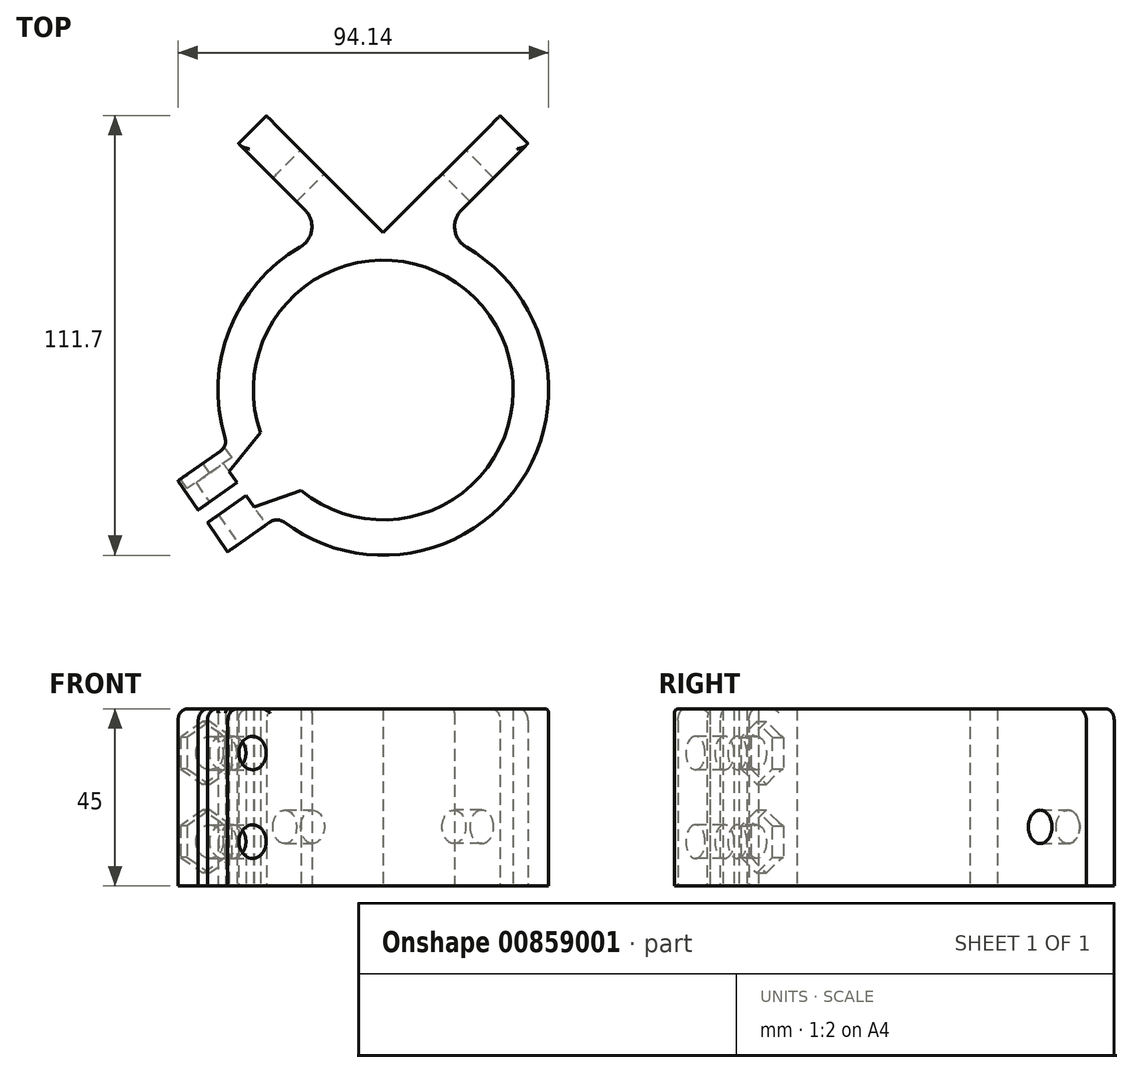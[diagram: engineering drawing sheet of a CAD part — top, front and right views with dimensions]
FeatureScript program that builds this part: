
annotation { "Feature Type Name" : "Feature", "Feature Type Description" : "" }
export const myFeature = defineFeature(function(context is Context, id is Id, definition is map)
    precondition{}
    {
        {
            var Q0;
            Q0=qCreatedBy(makeId("Top.planeOp"),FACE);
            var sketch = newSketch(context, id + "F0", { "sketchPlane" : qUnion([Q0])});
            skLineSegment(sketch, "E0", {"start": v(0, 0) * mm, "end": v(-29.7, 29.7) * mm});
            skLineSegment(sketch, "E1", {"start": v(0, 38.94) * mm, "end": v(0, 0) * mm, "construction": true});
            skLineSegment(sketch, "E2", {"start": v(-29.7, 29.7) * mm, "end": v(-36.77, 22.63) * mm});
            skLineSegment(sketch, "E3", {"start": v(-36.77, 22.63) * mm, "end": v(-13.8, -0.33) * mm});
            skLineSegment(sketch, "E4", {"start": v(0, 0) * mm, "end": v(0, -40) * mm, "construction": true});
            skArc(sketch, "E5", {"start": v(-25.84, -60.53) * mm, "mid": v(27.03, -21.07) * mm, "end": v(-28.13, -57.25) * mm});
            skArc(sketch, "E6", {"start": v(-33.22, -65.7) * mm, "mid": v(34.1, -64.53) * mm, "end": v(13.8, -0.33) * mm});
            skLineSegment(sketch, "E7", {"start": v(0, -40) * mm, "end": v(-34.4, -64.1) * mm, "construction": true});
            skLineSegment(sketch, "E8", {"start": v(-35.51, -62.42) * mm, "end": v(-46.98, -70.45) * mm});
            skLineSegment(sketch, "E9", {"start": v(-46.98, -70.45) * mm, "end": v(-52.14, -63.08) * mm});
            skLineSegment(sketch, "E10", {"start": v(-52.14, -63.08) * mm, "end": v(-39.51, -54.24) * mm});
            skLineSegment(sketch, "E11.MirrorCS", {"start": v(-44.69, -73.73) * mm, "end": v(-39.52, -81.1) * mm});
            skLineSegment(sketch, "E12.MirrorCS", {"start": v(-39.52, -81.1) * mm, "end": v(-26.9, -72.26) * mm});
            skLineSegment(sketch, "E13.MirrorCS", {"start": v(-33.22, -65.7) * mm, "end": v(-44.69, -73.73) * mm});
            skLineSegment(sketch, "E14", {"start": v(-35.51, -62.42) * mm, "end": v(-28.13, -57.25) * mm});
            skLineSegment(sketch, "E15.MirrorCS", {"start": v(-33.22, -65.7) * mm, "end": v(-25.84, -60.53) * mm});
            skLineSegment(sketch, "E16.MirrorCS", {"start": v(29.7, 29.7) * mm, "end": v(36.77, 22.63) * mm});
            skLineSegment(sketch, "E17.MirrorCS", {"start": v(0, 0) * mm, "end": v(29.7, 29.7) * mm});
            skLineSegment(sketch, "E18.MirrorCS", {"start": v(36.77, 22.63) * mm, "end": v(13.8, -0.33) * mm});
            skPoint(sketch, "E19.orphan", {"position": v(0, -14.14) * mm});
            skArc(sketch, "E20.trimOffspring", {"start": v(-13.8, -0.33) * mm, "mid": v(-39.65, -26.14) * mm, "end": v(-35.51, -62.42) * mm});
            skLineSegment(sketch, "E21", {"start": v(-31.17, -50.84) * mm, "end": v(-39.15, -60.7) * mm});
            skLineSegment(sketch, "E22.MirrorCS", {"start": v(-20.85, -65.58) * mm, "end": v(-32.84, -69.7) * mm});
            skLineSegment(sketch, "E23", {"start": v(-39.15, -60.7) * mm, "end": v(-32.84, -69.7) * mm});
            skSolve(sketch);
        }
        {
            var Q0;
            Q0=makeQuery(id+"F0.imprint","IMPRINT",FACE,{"disambiguationData":[TD([[makeQuery(id+"F0.imprint","IMPRINT",EDGE,{"derivedFrom":sQuery(id+"F0.wireOp",EDGE,"E0")}),1.0]])]});
            var Q1;
            {var subQ4=sQuery(id+"F0.wireOp",EDGE,"E9");Q1=makeQuery(id+"F0.imprint","IMPRINT",FACE,{"disambiguationData":[TD([[makeQuery(id+"F0.imprint","IMPRINT",EDGE,{"derivedFrom":subQ4}),-1.0]])]});}
            var Q2;
            {var subQ1=sQuery(id+"F0.wireOp",EDGE,"E11.MirrorCS");Q2=makeQuery(id+"F0.imprint","IMPRINT",FACE,{"disambiguationData":[TD([[makeQuery(id+"F0.imprint","IMPRINT",EDGE,{"derivedFrom":subQ1}),1.0]])]});}
            extrude(context, id + "F1", {"entities" : qUnion([Q0, Q1, Q2]), "depth" : 45 * mm, "offsetDistance" : 25 * mm});
        }
        {
            var Q0;
            Q0=makeQuery(id+"F1.opExtrude","SWEPT_FACE",FACE,{"disambiguationData":[OSD([sQuery(id+"F0.wireOp",EDGE,"E17.MirrorCS")])]});
            var sketch = newSketch(context, id + "F2", { "sketchPlane" : qUnion([Q0])});
            skLineSegment(sketch, "E24", {"start": v(0, 15) * mm, "end": v(-50.8, 15) * mm, "construction": true});
            skCircle(sketch, "E25", {"center": v(-25.4, 15) * mm, "radius": 4.25 * mm});
            skSolve(sketch);
        }
        {
            var Q0;
            Q0=qSketchRegion(id+"F2",true);
            extrude(context, id + "F3", {"entities" : qUnion([Q0]), "operationType" : NewBodyOperationType.REMOVE, "endBound" : BoundingType.UP_TO_NEXT, "oppositeDirection" : true, "depth" : 25 * mm, "offsetDistance" : 25 * mm});
        }
        {
            var Q0;
            Q0=makeQuery(id+"F1.opExtrude","SWEPT_FACE",FACE,{"disambiguationData":[OSD([sQuery(id+"F0.wireOp",EDGE,"E0")])]});
            var sketch = newSketch(context, id + "F4", { "sketchPlane" : qUnion([Q0])});
            skLineSegment(sketch, "E26", {"start": v(0, 15) * mm, "end": v(50.8, 15) * mm, "construction": true});
            skCircle(sketch, "E27", {"center": v(25.4, 15) * mm, "radius": 4.25 * mm});
            skSolve(sketch);
        }
        {
            var Q0;
            Q0=qSketchRegion(id+"F4",true);
            extrude(context, id + "F5", {"entities" : qUnion([Q0]), "operationType" : NewBodyOperationType.REMOVE, "endBound" : BoundingType.UP_TO_NEXT, "oppositeDirection" : true, "depth" : 25 * mm, "offsetDistance" : 25 * mm});
        }
        {
            var Q0;
            Q0=makeQuery(id+"F1.opExtrude","SWEPT_FACE",FACE,{"disambiguationData":[OSD([sQuery(id+"F0.wireOp",EDGE,"E12.MirrorCS")])]});
            var sketch = newSketch(context, id + "F6", { "sketchPlane" : qUnion([Q0])});
            skLineSegment(sketch, "E28", {"start": v(-71.19, 45) * mm, "end": v(-71.19, 0) * mm, "construction": true});
            skLineSegment(sketch, "E29", {"start": v(-78.9, 22.5) * mm, "end": v(-63.48, 22.5) * mm, "construction": true});
            skLineSegment(sketch, "E30", {"start": v(-78.9, 22.5) * mm, "end": v(-63.48, 45) * mm, "construction": true});
            skCircle(sketch, "E31", {"center": v(-71.19, 33.75) * mm, "radius": 4.25 * mm});
            skCircle(sketch, "E32.MirrorC", {"center": v(-71.19, 11.25) * mm, "radius": 4.25 * mm});
            skLineSegment(sketch, "E33.MirrorCS", {"start": v(-78.9, 22.5) * mm, "end": v(-63.48, 0) * mm, "construction": true});
            skSolve(sketch);
        }
        {
            var Q0;
            Q0=qSketchRegion(id+"F6",true);
            var Q1;
            Q1=makeQuery(id+"F1.opExtrude","SWEPT_FACE",FACE,{"disambiguationData":[OSD([sQuery(id+"F0.wireOp",EDGE,"E10")])]});
            extrude(context, id + "F7", {"entities" : qUnion([Q0]), "operationType" : NewBodyOperationType.REMOVE, "endBound" : BoundingType.UP_TO_SURFACE, "oppositeDirection" : true, "depth" : 25 * mm, "endBoundEntityFace" : qUnion([Q1]), "offsetDistance" : 25 * mm});
        }
        {
            var Q0;
            Q0=makeQuery(id+"F1.opExtrude","SWEPT_FACE",FACE,{"disambiguationData":[OSD([sQuery(id+"F0.wireOp",EDGE,"E10")])]});
            var sketch = newSketch(context, id + "F8", { "sketchPlane" : qUnion([Q0])});
            skCircle(sketch, "E34.cCircle", {"center": v(71.19, 33.75) * mm, "radius": 6.92 * mm, "construction": true});
            skLineSegment(sketch, "E34.0", {"start": v(71.19, 41.75) * mm, "end": v(78.11, 37.75) * mm});
            skLineSegment(sketch, "E34.1", {"start": v(78.11, 37.75) * mm, "end": v(78.11, 29.75) * mm});
            skLineSegment(sketch, "E34.2", {"start": v(78.11, 29.75) * mm, "end": v(71.19, 25.75) * mm});
            skLineSegment(sketch, "E34.3", {"start": v(71.19, 25.75) * mm, "end": v(64.26, 29.75) * mm});
            skLineSegment(sketch, "E34.4", {"start": v(64.26, 29.75) * mm, "end": v(64.26, 37.75) * mm});
            skLineSegment(sketch, "E34.5", {"start": v(64.26, 37.75) * mm, "end": v(71.19, 41.75) * mm});
            skPoint(sketch, "E34.0.midPoint", {"position": v(74.65, 39.75) * mm});
            skCircle(sketch, "E35.cCircle", {"center": v(71.19, 11.25) * mm, "radius": 6.92 * mm, "construction": true});
            skLineSegment(sketch, "E35.0", {"start": v(64.26, 15.25) * mm, "end": v(71.19, 19.25) * mm});
            skLineSegment(sketch, "E35.1", {"start": v(71.19, 19.25) * mm, "end": v(78.11, 15.25) * mm});
            skLineSegment(sketch, "E35.2", {"start": v(78.11, 15.25) * mm, "end": v(78.11, 7.25) * mm});
            skLineSegment(sketch, "E35.3", {"start": v(78.11, 7.25) * mm, "end": v(71.19, 3.25) * mm});
            skLineSegment(sketch, "E35.4", {"start": v(71.19, 3.25) * mm, "end": v(64.26, 7.25) * mm});
            skLineSegment(sketch, "E35.5", {"start": v(64.26, 7.25) * mm, "end": v(64.26, 15.25) * mm});
            skPoint(sketch, "E35.0.midPoint", {"position": v(67.72, 17.25) * mm});
            skSolve(sketch);
        }
        {
            var Q0;
            Q0=qSketchRegion(id+"F8",true);
            extrude(context, id + "F9", {"entities" : qUnion([Q0]), "operationType" : NewBodyOperationType.REMOVE, "oppositeDirection" : true, "depth" : 3 * mm, "offsetDistance" : 25 * mm});
        }
        {
            var Q0;
            Q0=makeQuery(id+"F1.opExtrude","SWEPT_EDGE",EDGE,{"disambiguationData":[OSD([sQuery(id+"F0.wireOp",EDGE,"E3"),sQuery(id+"F0.wireOp",EDGE,"E20.trimOffspring")])]});
            var Q1;
            Q1=makeQuery(id+"F1.opExtrude","SWEPT_EDGE",EDGE,{"disambiguationData":[OSD([sQuery(id+"F0.wireOp",EDGE,"E6"),sQuery(id+"F0.wireOp",EDGE,"E18.MirrorCS")])]});
            fillet(context, id + "F10", {"entities" : qUnion([Q0, Q1]), "radius" : 6 * mm, "tangentPropagation" : true, "allowEdgeOverflow" : false});
        }
        {
            var Q0;
            Q0=makeQuery(id+"F1.opExtrude","CAP_EDGE",EDGE,{"disambiguationData":[OSD([sQuery(id+"F0.wireOp",EDGE,"E9")])],"isStart":false});
            var Q1;
            Q1=makeQuery(id+"F1.opExtrude","CAP_EDGE",EDGE,{"disambiguationData":[OSD([sQuery(id+"F0.wireOp",EDGE,"E11.MirrorCS")])],"isStart":false});
            var Q2;
            Q2=makeQuery(id+"F1.opExtrude","CAP_EDGE",EDGE,{"disambiguationData":[OSD([sQuery(id+"F0.wireOp",EDGE,"E2")])],"isStart":false});
            var Q3;
            Q3=makeQuery(id+"F1.opExtrude","CAP_EDGE",EDGE,{"disambiguationData":[OSD([sQuery(id+"F0.wireOp",EDGE,"E16.MirrorCS")])],"isStart":false});
            var Q4;
            Q4=makeQuery(id+"F1.opExtrude","SWEPT_EDGE",EDGE,{"disambiguationData":[OSD([sQuery(id+"F0.wireOp",EDGE,"E10"),sQuery(id+"F0.wireOp",EDGE,"E20.trimOffspring")])]});
            var Q5;
            Q5=makeQuery(id+"F1.opExtrude","SWEPT_EDGE",EDGE,{"disambiguationData":[OSD([sQuery(id+"F0.wireOp",EDGE,"E6"),sQuery(id+"F0.wireOp",EDGE,"E12.MirrorCS")])]});
            fillet(context, id + "F11", {"entities" : qUnion([Q0, Q1, Q2, Q3, Q4, Q5]), "radius" : 3 * mm, "tangentPropagation" : true, "allowEdgeOverflow" : false});
        }
        {
            var Q0;
            Q0=makeQuery(id+"F1.opExtrude","CAP_EDGE",EDGE,{"disambiguationData":[OSD([sQuery(id+"F0.wireOp",EDGE,"E6")])],"isStart":false});
            var Q1;
            {var subQ0=sQuery(id+"F0.wireOp",EDGE,"E12.MirrorCS");var subQ1=sQuery(id+"F0.wireOp",EDGE,"E6");Q1=makeQuery(id+"F11.opFillet","BLEND_EDGE",EDGE,{"blendedFrom":[makeQuery(id+"F1.opExtrude","SWEPT_EDGE",EDGE,{"disambiguationData":[OSD([subQ1,subQ0])]}),makeQuery(id+"F1.opExtrude","CAP_FACE",FACE,{"disambiguationData":[OSD([sQuery(id+"F0.wireOp",EDGE,"E0"),sQuery(id+"F0.wireOp",EDGE,"E2"),sQuery(id+"F0.wireOp",EDGE,"E3"),sQuery(id+"F0.wireOp",EDGE,"E5"),subQ1,sQuery(id+"F0.wireOp",EDGE,"E8"),sQuery(id+"F0.wireOp",EDGE,"E9"),sQuery(id+"F0.wireOp",EDGE,"E10"),sQuery(id+"F0.wireOp",EDGE,"E11.MirrorCS"),subQ0,sQuery(id+"F0.wireOp",EDGE,"E13.MirrorCS"),sQuery(id+"F0.wireOp",EDGE,"E16.MirrorCS"),sQuery(id+"F0.wireOp",EDGE,"E17.MirrorCS"),sQuery(id+"F0.wireOp",EDGE,"E18.MirrorCS"),sQuery(id+"F0.wireOp",EDGE,"E20.trimOffspring"),sQuery(id+"F0.wireOp",EDGE,"E21"),sQuery(id+"F0.wireOp",EDGE,"E22.MirrorCS"),sQuery(id+"F0.wireOp",EDGE,"E23")])],"isStart":false})],"blendedInto":[makeQuery(id+"F1.opExtrude","CAP_FACE",FACE,{"disambiguationData":[OSD([sQuery(id+"F0.wireOp",EDGE,"E0"),sQuery(id+"F0.wireOp",EDGE,"E2"),sQuery(id+"F0.wireOp",EDGE,"E3"),sQuery(id+"F0.wireOp",EDGE,"E5"),subQ1,sQuery(id+"F0.wireOp",EDGE,"E8"),sQuery(id+"F0.wireOp",EDGE,"E9"),sQuery(id+"F0.wireOp",EDGE,"E10"),sQuery(id+"F0.wireOp",EDGE,"E11.MirrorCS"),subQ0,sQuery(id+"F0.wireOp",EDGE,"E13.MirrorCS"),sQuery(id+"F0.wireOp",EDGE,"E16.MirrorCS"),sQuery(id+"F0.wireOp",EDGE,"E17.MirrorCS"),sQuery(id+"F0.wireOp",EDGE,"E18.MirrorCS"),sQuery(id+"F0.wireOp",EDGE,"E20.trimOffspring"),sQuery(id+"F0.wireOp",EDGE,"E21"),sQuery(id+"F0.wireOp",EDGE,"E22.MirrorCS"),sQuery(id+"F0.wireOp",EDGE,"E23")])],"isStart":false})]});}
            var Q2;
            {var subQ0=sQuery(id+"F0.wireOp",EDGE,"E20.trimOffspring");var subQ1=sQuery(id+"F0.wireOp",EDGE,"E3");Q2=makeQuery(id+"F10.opFillet","BLEND_EDGE",EDGE,{"blendedFrom":[makeQuery(id+"F1.opExtrude","SWEPT_EDGE",EDGE,{"disambiguationData":[OSD([subQ1,subQ0])]}),makeQuery(id+"F1.opExtrude","CAP_FACE",FACE,{"disambiguationData":[OSD([sQuery(id+"F0.wireOp",EDGE,"E0"),sQuery(id+"F0.wireOp",EDGE,"E2"),subQ1,sQuery(id+"F0.wireOp",EDGE,"E5"),sQuery(id+"F0.wireOp",EDGE,"E6"),sQuery(id+"F0.wireOp",EDGE,"E8"),sQuery(id+"F0.wireOp",EDGE,"E9"),sQuery(id+"F0.wireOp",EDGE,"E10"),sQuery(id+"F0.wireOp",EDGE,"E11.MirrorCS"),sQuery(id+"F0.wireOp",EDGE,"E12.MirrorCS"),sQuery(id+"F0.wireOp",EDGE,"E13.MirrorCS"),sQuery(id+"F0.wireOp",EDGE,"E16.MirrorCS"),sQuery(id+"F0.wireOp",EDGE,"E17.MirrorCS"),sQuery(id+"F0.wireOp",EDGE,"E18.MirrorCS"),subQ0,sQuery(id+"F0.wireOp",EDGE,"E21"),sQuery(id+"F0.wireOp",EDGE,"E22.MirrorCS"),sQuery(id+"F0.wireOp",EDGE,"E23")])],"isStart":false})],"blendedInto":[makeQuery(id+"F1.opExtrude","CAP_FACE",FACE,{"disambiguationData":[OSD([sQuery(id+"F0.wireOp",EDGE,"E0"),sQuery(id+"F0.wireOp",EDGE,"E2"),subQ1,sQuery(id+"F0.wireOp",EDGE,"E5"),sQuery(id+"F0.wireOp",EDGE,"E6"),sQuery(id+"F0.wireOp",EDGE,"E8"),sQuery(id+"F0.wireOp",EDGE,"E9"),sQuery(id+"F0.wireOp",EDGE,"E10"),sQuery(id+"F0.wireOp",EDGE,"E11.MirrorCS"),sQuery(id+"F0.wireOp",EDGE,"E12.MirrorCS"),sQuery(id+"F0.wireOp",EDGE,"E13.MirrorCS"),sQuery(id+"F0.wireOp",EDGE,"E16.MirrorCS"),sQuery(id+"F0.wireOp",EDGE,"E17.MirrorCS"),sQuery(id+"F0.wireOp",EDGE,"E18.MirrorCS"),subQ0,sQuery(id+"F0.wireOp",EDGE,"E21"),sQuery(id+"F0.wireOp",EDGE,"E22.MirrorCS"),sQuery(id+"F0.wireOp",EDGE,"E23")])],"isStart":false})]});}
            var Q3;
            Q3=makeQuery(id+"F1.opExtrude","CAP_EDGE",EDGE,{"disambiguationData":[OSD([sQuery(id+"F0.wireOp",EDGE,"E3")])],"isStart":false});
            var Q4;
            Q4=makeQuery(id+"F1.opExtrude","CAP_EDGE",EDGE,{"disambiguationData":[OSD([sQuery(id+"F0.wireOp",EDGE,"E18.MirrorCS")])],"isStart":false});
            var Q5;
            {var subQ0=sQuery(id+"F0.wireOp",EDGE,"E18.MirrorCS");var subQ1=sQuery(id+"F0.wireOp",EDGE,"E6");Q5=makeQuery(id+"F10.opFillet","BLEND_EDGE",EDGE,{"blendedFrom":[makeQuery(id+"F1.opExtrude","SWEPT_EDGE",EDGE,{"disambiguationData":[OSD([subQ1,subQ0])]}),makeQuery(id+"F1.opExtrude","CAP_FACE",FACE,{"disambiguationData":[OSD([sQuery(id+"F0.wireOp",EDGE,"E0"),sQuery(id+"F0.wireOp",EDGE,"E2"),sQuery(id+"F0.wireOp",EDGE,"E3"),sQuery(id+"F0.wireOp",EDGE,"E5"),subQ1,sQuery(id+"F0.wireOp",EDGE,"E8"),sQuery(id+"F0.wireOp",EDGE,"E9"),sQuery(id+"F0.wireOp",EDGE,"E10"),sQuery(id+"F0.wireOp",EDGE,"E11.MirrorCS"),sQuery(id+"F0.wireOp",EDGE,"E12.MirrorCS"),sQuery(id+"F0.wireOp",EDGE,"E13.MirrorCS"),sQuery(id+"F0.wireOp",EDGE,"E16.MirrorCS"),sQuery(id+"F0.wireOp",EDGE,"E17.MirrorCS"),subQ0,sQuery(id+"F0.wireOp",EDGE,"E20.trimOffspring"),sQuery(id+"F0.wireOp",EDGE,"E21"),sQuery(id+"F0.wireOp",EDGE,"E22.MirrorCS"),sQuery(id+"F0.wireOp",EDGE,"E23")])],"isStart":false})],"blendedInto":[makeQuery(id+"F1.opExtrude","CAP_FACE",FACE,{"disambiguationData":[OSD([sQuery(id+"F0.wireOp",EDGE,"E0"),sQuery(id+"F0.wireOp",EDGE,"E2"),sQuery(id+"F0.wireOp",EDGE,"E3"),sQuery(id+"F0.wireOp",EDGE,"E5"),subQ1,sQuery(id+"F0.wireOp",EDGE,"E8"),sQuery(id+"F0.wireOp",EDGE,"E9"),sQuery(id+"F0.wireOp",EDGE,"E10"),sQuery(id+"F0.wireOp",EDGE,"E11.MirrorCS"),sQuery(id+"F0.wireOp",EDGE,"E12.MirrorCS"),sQuery(id+"F0.wireOp",EDGE,"E13.MirrorCS"),sQuery(id+"F0.wireOp",EDGE,"E16.MirrorCS"),sQuery(id+"F0.wireOp",EDGE,"E17.MirrorCS"),subQ0,sQuery(id+"F0.wireOp",EDGE,"E20.trimOffspring"),sQuery(id+"F0.wireOp",EDGE,"E21"),sQuery(id+"F0.wireOp",EDGE,"E22.MirrorCS"),sQuery(id+"F0.wireOp",EDGE,"E23")])],"isStart":false})]});}
            var Q6;
            {var subQ0=sQuery(id+"F0.wireOp",EDGE,"E20.trimOffspring");var subQ1=sQuery(id+"F0.wireOp",EDGE,"E10");Q6=makeQuery(id+"F11.opFillet","BLEND_EDGE",EDGE,{"blendedFrom":[makeQuery(id+"F1.opExtrude","SWEPT_EDGE",EDGE,{"disambiguationData":[OSD([subQ1,subQ0])]}),makeQuery(id+"F1.opExtrude","CAP_FACE",FACE,{"disambiguationData":[OSD([sQuery(id+"F0.wireOp",EDGE,"E0"),sQuery(id+"F0.wireOp",EDGE,"E2"),sQuery(id+"F0.wireOp",EDGE,"E3"),sQuery(id+"F0.wireOp",EDGE,"E5"),sQuery(id+"F0.wireOp",EDGE,"E6"),sQuery(id+"F0.wireOp",EDGE,"E8"),sQuery(id+"F0.wireOp",EDGE,"E9"),subQ1,sQuery(id+"F0.wireOp",EDGE,"E11.MirrorCS"),sQuery(id+"F0.wireOp",EDGE,"E12.MirrorCS"),sQuery(id+"F0.wireOp",EDGE,"E13.MirrorCS"),sQuery(id+"F0.wireOp",EDGE,"E16.MirrorCS"),sQuery(id+"F0.wireOp",EDGE,"E17.MirrorCS"),sQuery(id+"F0.wireOp",EDGE,"E18.MirrorCS"),subQ0,sQuery(id+"F0.wireOp",EDGE,"E21"),sQuery(id+"F0.wireOp",EDGE,"E22.MirrorCS"),sQuery(id+"F0.wireOp",EDGE,"E23")])],"isStart":false})],"blendedInto":[makeQuery(id+"F1.opExtrude","CAP_FACE",FACE,{"disambiguationData":[OSD([sQuery(id+"F0.wireOp",EDGE,"E0"),sQuery(id+"F0.wireOp",EDGE,"E2"),sQuery(id+"F0.wireOp",EDGE,"E3"),sQuery(id+"F0.wireOp",EDGE,"E5"),sQuery(id+"F0.wireOp",EDGE,"E6"),sQuery(id+"F0.wireOp",EDGE,"E8"),sQuery(id+"F0.wireOp",EDGE,"E9"),subQ1,sQuery(id+"F0.wireOp",EDGE,"E11.MirrorCS"),sQuery(id+"F0.wireOp",EDGE,"E12.MirrorCS"),sQuery(id+"F0.wireOp",EDGE,"E13.MirrorCS"),sQuery(id+"F0.wireOp",EDGE,"E16.MirrorCS"),sQuery(id+"F0.wireOp",EDGE,"E17.MirrorCS"),sQuery(id+"F0.wireOp",EDGE,"E18.MirrorCS"),subQ0,sQuery(id+"F0.wireOp",EDGE,"E21"),sQuery(id+"F0.wireOp",EDGE,"E22.MirrorCS"),sQuery(id+"F0.wireOp",EDGE,"E23")])],"isStart":false})]});}
            var Q7;
            Q7=makeQuery(id+"F1.opExtrude","CAP_EDGE",EDGE,{"disambiguationData":[OSD([sQuery(id+"F0.wireOp",EDGE,"E20.trimOffspring")])],"isStart":false});
            fillet(context, id + "F12", {"entities" : qUnion([Q0, Q1, Q2, Q3, Q4, Q5, Q6, Q7]), "radius" : 1 * mm, "allowEdgeOverflow" : false});
        }
    });
